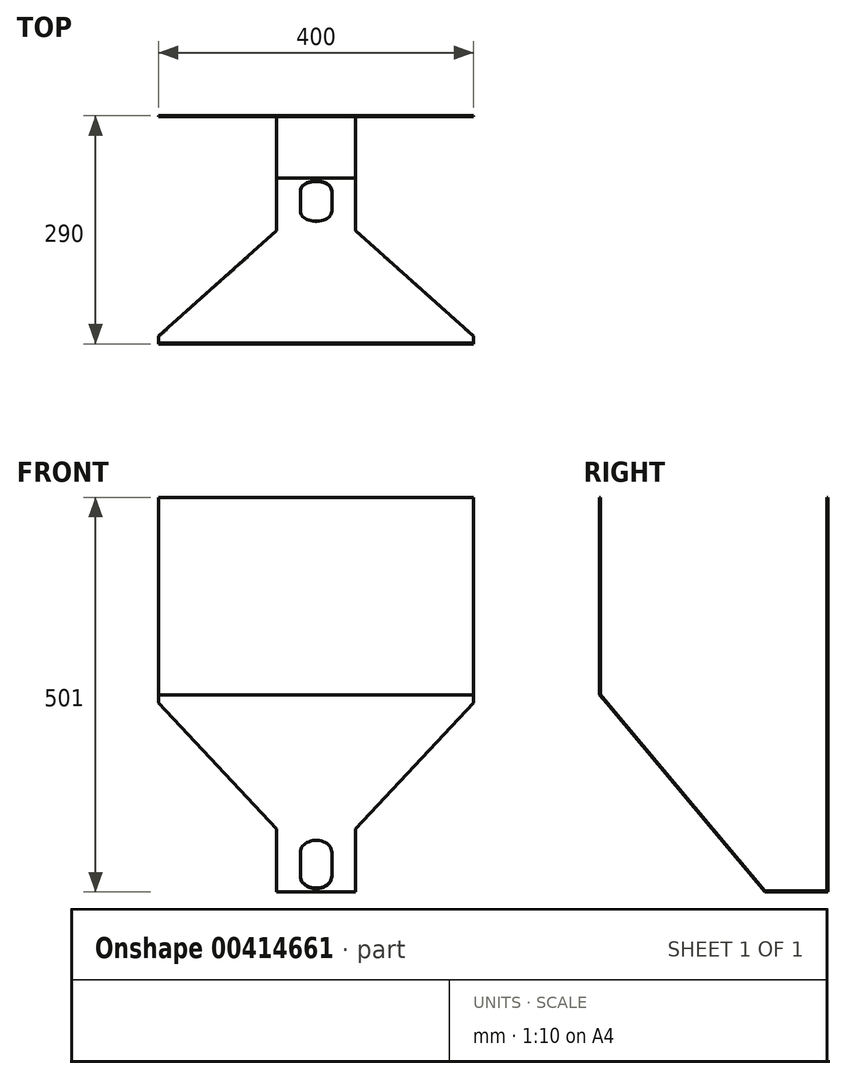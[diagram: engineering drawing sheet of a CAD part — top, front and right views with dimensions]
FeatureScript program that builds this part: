
annotation { "Feature Type Name" : "Feature", "Feature Type Description" : "" }
export const myFeature = defineFeature(function(context is Context, id is Id, definition is map)
    precondition{}
    {
        {
            var Q0;
            Q0=qCreatedBy(makeId("Right.planeOp"),FACE);
            var sketch = newSketch(context, id + "F0", { "sketchPlane" : qUnion([Q0])});
            skLineSegment(sketch, "E0", {"start": v(0, 0) * mm, "end": v(-80, 0) * mm});
            skLineSegment(sketch, "E1", {"start": v(-80, 0) * mm, "end": v(-290, 250.27) * mm});
            skLineSegment(sketch, "E2", {"start": v(-290, 250.27) * mm, "end": v(-290, 501) * mm});
            skLineSegment(sketch, "E3", {"start": v(0, 0) * mm, "end": v(0, 501) * mm});
            skLineSegment(sketch, "E4.0", {"start": v(-289, 250.63) * mm, "end": v(-289, 501) * mm});
            skLineSegment(sketch, "E4.1", {"start": v(-79.53, 1) * mm, "end": v(-289, 250.63) * mm});
            skLineSegment(sketch, "E4.2", {"start": v(-1, 1) * mm, "end": v(-79.53, 1) * mm});
            skLineSegment(sketch, "E4.3", {"start": v(-1, 1) * mm, "end": v(-1, 501) * mm});
            skLineSegment(sketch, "E5", {"start": v(-290, 501) * mm, "end": v(-289, 501) * mm});
            skLineSegment(sketch, "E6", {"start": v(-1, 501) * mm, "end": v(0, 501) * mm});
            skSolve(sketch);
        }
        {
            var Q0;
            Q0=makeQuery(id+"F0.imprint","IMPRINT",FACE,{"disambiguationData":[TD([[makeQuery(id+"F0.imprint","IMPRINT",EDGE,{"derivedFrom":sQuery(id+"F0.wireOp",EDGE,"E0")}),-1.0]])]});
            extrude(context, id + "F1", {"entities" : qUnion([Q0]), "oppositeDirection" : true, "depth" : 400 * mm});
        }
        {
            var Q0;
            Q0=makeQuery(id+"F1.opExtrude","SWEPT_FACE",FACE,{"disambiguationData":[OSD([sQuery(id+"F0.wireOp",EDGE,"E3")])]});
            var sketch = newSketch(context, id + "F2", { "sketchPlane" : qUnion([Q0])});
            skLineSegment(sketch, "E7", {"start": v(400, 240) * mm, "end": v(250, 80) * mm});
            skLineSegment(sketch, "E8", {"start": v(250, 80) * mm, "end": v(250, 0) * mm});
            skLineSegment(sketch, "E9", {"start": v(200, 0) * mm, "end": v(200, 198.96) * mm, "construction": true});
            skLineSegment(sketch, "E10.MirrorCS", {"start": v(0, 240) * mm, "end": v(150, 80) * mm});
            skLineSegment(sketch, "E11.MirrorCS", {"start": v(150, 80) * mm, "end": v(150, 0) * mm});
            skSolve(sketch);
        }
        {
            var Q0;
            {var subQ0=sQuery(id+"F2.wireOp",EDGE,"Qxc1O4Ee-7d8E-R3Kk-48Ti-2GcufYxCDCyJ");Q0=makeQuery(id+"F2.imprint","IMPRINT",FACE,{"disambiguationData":[TD([[makeQuery(id+"F2.imprint","IMPRINT",EDGE,{"derivedFrom":subQ0}),-1.0]])]});}
            var Q1;
            {var subQ0=sQuery(id+"F2.wireOp",EDGE,"E7");Q1=makeQuery(id+"F2.imprint","IMPRINT",FACE,{"disambiguationData":[TD([[makeQuery(id+"F2.imprint","IMPRINT",EDGE,{"derivedFrom":subQ0}),1.0]])]});}
            var Q2;
            {var subQ0=sQuery(id+"F2.wireOp",EDGE,"E10.MirrorCS");Q2=makeQuery(id+"F2.imprint","IMPRINT",FACE,{"disambiguationData":[TD([[makeQuery(id+"F2.imprint","IMPRINT",EDGE,{"derivedFrom":subQ0}),-1.0]])]});}
            extrude(context, id + "F3", {"entities" : qUnion([Q0, Q1, Q2]), "operationType" : NewBodyOperationType.REMOVE, "endBound" : BoundingType.THROUGH_ALL, "oppositeDirection" : true, "depth" : 25 * mm});
        }
        {
            var Q0;
            Q0=makeQuery(id+"F1.opExtrude","SWEPT_FACE",FACE,{"disambiguationData":[OSD([sQuery(id+"F0.wireOp",EDGE,"E4.1")])]});
            var sketch = newSketch(context, id + "F4", { "sketchPlane" : qUnion([Q0])});
            skLineSegment(sketch, "E12", {"start": v(200, 51.89) * mm, "end": v(200, 160.41) * mm, "construction": true});
            skArc(sketch, "E13", {"start": v(180, 76.89) * mm, "mid": v(200, 56.89) * mm, "end": v(220, 76.89) * mm});
            skArc(sketch, "E14", {"start": v(220, 116.89) * mm, "mid": v(200, 136.89) * mm, "end": v(180, 116.89) * mm});
            skLineSegment(sketch, "E15", {"start": v(180, 116.89) * mm, "end": v(180, 76.89) * mm});
            skLineSegment(sketch, "E16", {"start": v(220, 116.89) * mm, "end": v(220, 76.89) * mm});
            skSolve(sketch);
        }
        {
            var Q0;
            Q0=makeQuery(id+"F4.imprint","IMPRINT",FACE,{"disambiguationData":[TD([[makeQuery(id+"F4.imprint","IMPRINT",EDGE,{"derivedFrom":sQuery(id+"F4.wireOp",EDGE,"E13")}),1.0]])]});
            extrude(context, id + "F5", {"entities" : qUnion([Q0]), "operationType" : NewBodyOperationType.REMOVE, "endBound" : BoundingType.THROUGH_ALL, "oppositeDirection" : true, "depth" : 25 * mm});
        }
    });
